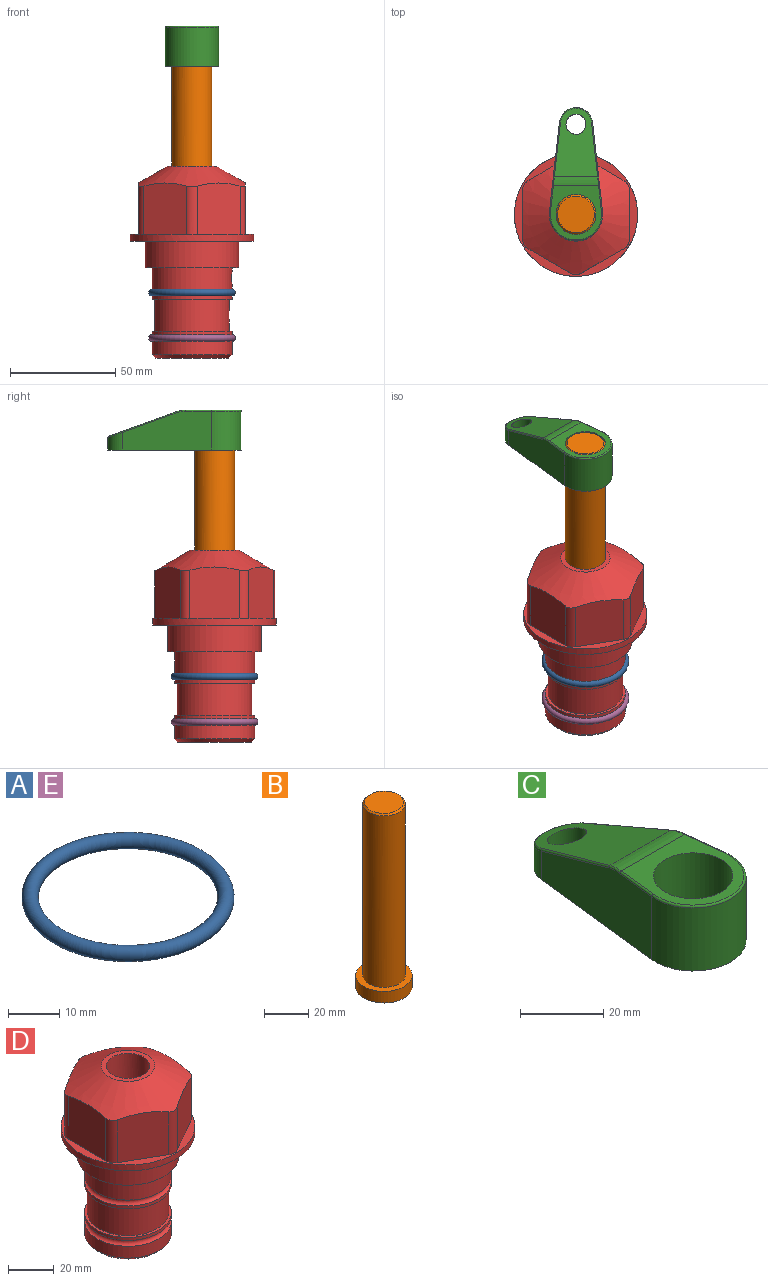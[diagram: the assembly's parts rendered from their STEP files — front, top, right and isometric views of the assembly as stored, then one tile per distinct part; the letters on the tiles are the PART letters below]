
ASSEMBLY  parts=5 mates=3
PART A: 1 faces, bbox 44.7x44.7x3.2 mm
  f0: torus R=19.05mm, axis (0,0,1), area 1193.9mm2
PART B: 6 faces, bbox 25.4x25.4x101.6 mm
  f0: plane 17.46x17.46mm, normal (0,0,1), area 239.5mm2, adj f5
  f1: plane 25.4x25.4mm, normal (0,0,-1), area 506.7mm2, adj f2
  f2: cylinder r=12.7mm len=25.4mm, axis (0,0,1), area 506.7mm2, adj f1,f3
  f3: plane 25.4x25.4mm, normal (0,0,1), area 221.7mm2, adj f2,f4
  f4: cylinder r=9.53mm len=94.46mm, axis (0,0,1), area 5653mm2, adj f3,f5
  f5: cone r=8.73mm half-angle=45deg, axis (0,0,-1), area 64.4mm2, adj f0,f4
PART C: 44 faces, bbox 27.5x64.5x19.1 mm
  f0: plane 2.3x0.95mm, normal (0,0,-1), area 1mm2, adj f25,f30,f34
  f1: plane 63.5x25.4mm, normal (0,0,-1), area 561.7mm2, adj f2,f3,f4,f5,f6,f7,f19,f20
  f2: cylinder r=12.7mm len=25.4mm, axis (0,0,-1), area 792.2mm2, adj f1,f3,f5,f13
  f3: plane 42.33x18.54mm, normal (0.99,0.11,0), area 647mm2, adj f1,f2,f4,f11,f12,f14
  f4: cylinder r=7.94mm len=15.78mm, axis (0,0,-1), area 158.6mm2, adj f1,f3,f5,f16
  f5: plane 42.33x18.54mm, normal (-0.99,0.11,0), area 647mm2, adj f1,f2,f4,f15,f17,f18
  f6: cylinder r=9.53mm len=19.05mm, axis (0,0,-1), area 1140.1mm2, adj f1,f8
  f7: cylinder r=4.76mm len=10.98mm, axis (0,0,-1), area 276.1mm2, adj f1,f9
  f8: plane 25.83x24.38mm, normal (0,0,1), area 262.2mm2, adj f6,f10,f11,f13,f15
  f9: plane 32.49x20.55mm, normal (0,0.34,0.94), area 489.9mm2, adj f7,f10,f14,f16,f18
  f10: cylinder r=12.7mm len=21.49mm, axis (-1,0,0), area 93.2mm2, adj f8,f9,f12,f17
  f11: cylinder r=0.51mm len=12.34mm, axis (0.11,-0.99,0), area 9.9mm2, adj f3,f8,f12,f13
  f12: bspline ~7.62x1.64mm, area 3.5mm2, adj f3,f10,f11,f14
  f13: torus R=12.19mm, axis (0,0,1), area 33.6mm2, adj f2,f8,f11,f15
  f14: cylinder r=0.51mm len=26.01mm, axis (0.1,-0.93,0.34), area 21.6mm2, adj f3,f9,f12,f16
  f15: cylinder r=0.51mm len=12.34mm, axis (0.11,0.99,0), area 9.9mm2, adj f5,f8,f13,f17
  f16: bspline ~15.78x7.05mm, area 15.7mm2, adj f4,f9,f14,f18
  f17: bspline ~7.62x1.64mm, area 3.5mm2, adj f5,f10,f15,f18
  f18: cylinder r=0.51mm len=26.01mm, axis (0.1,0.93,-0.34), area 21.6mm2, adj f5,f9,f16,f17
  f19: plane 21.6x14.29mm, normal (-0.99,-0.11,0), area 242.6mm2, adj f1,f26,f28,f34,f36,f38
  f20: plane 21.6x14.29mm, normal (0.99,-0.11,0), area 242.6mm2, adj f1,f27,f29,f37,f39,f41
  f21: cylinder r=12.7mm len=14.29mm, axis (0,0,-1), area 173.2mm2, adj f1,f26,f27,f30,f31,f33
  f22: cylinder r=7.94mm len=7.63mm, axis (0,0,-1), area 53.8mm2, adj f1,f28,f29,f42
  f23: plane 2.3x0.95mm, normal (0,0,-1), area 1mm2, adj f25,f33,f37
  f24: plane 17.94x12.32mm, normal (0,-0.34,-0.94), area 191.2mm2, adj f25,f38,f41,f42
  f25: cylinder r=9.53mm len=12.93mm, axis (-1,0,0), area 37.5mm2, adj f0,f23,f24,f31,f36,f39
  f26: cylinder r=1.59mm len=14.29mm, axis (0,0,-1), area 49mm2, adj f1,f19,f21,f32
  f27: cylinder r=1.59mm len=14.29mm, axis (0,0,-1), area 49mm2, adj f1,f20,f21,f35
  f28: cylinder r=1.59mm len=7.28mm, axis (0,0,-1), area 22.1mm2, adj f1,f19,f22,f40
  f29: cylinder r=1.59mm len=7.28mm, axis (0,0,-1), area 22.1mm2, adj f1,f20,f22,f43
  f30: torus R=14.29mm, axis (0,0,1), area 5.8mm2, adj f0,f21,f31,f32
  f31: bspline ~11.06x2.73mm, area 20.8mm2, adj f21,f25,f30,f33
  f32: sphere r=1.59mm, area 5.4mm2, adj f26,f30,f34
  f33: torus R=14.29mm, axis (0,0,1), area 5.8mm2, adj f21,f23,f31,f35
  f34: cylinder r=1.59mm len=1.68mm, axis (-0.11,0.99,0), area 2.4mm2, adj f0,f19,f32,f36
  f35: sphere r=1.59mm, area 5.4mm2, adj f27,f33,f37
  f36: bspline ~5.82x2.33mm, area 7.7mm2, adj f19,f25,f34,f38
  f37: cylinder r=1.59mm len=1.68mm, axis (0.11,0.99,0), area 2.4mm2, adj f20,f23,f35,f39
  f38: cylinder r=1.59mm len=18.33mm, axis (0.1,-0.93,0.34), area 46.7mm2, adj f19,f24,f36,f40
  f39: bspline ~5.82x2.33mm, area 7.7mm2, adj f20,f25,f37,f41
  f40: sphere r=1.59mm, area 3.6mm2, adj f28,f38,f42
  f41: cylinder r=1.59mm len=18.33mm, axis (0.1,0.93,-0.34), area 46.7mm2, adj f20,f24,f39,f43
  f42: bspline ~8.31x1.84mm, area 15.3mm2, adj f22,f24,f40,f43
  f43: sphere r=1.59mm, area 3.6mm2, adj f29,f41,f42
PART D: 36 faces, bbox 58.7x58.7x91.2 mm
  f0: cylinder r=17.78mm len=35.56mm, axis (0,0,1), area 1670.8mm2, adj f23,f24,f31
  f1: cylinder r=19.05mm len=38.1mm, axis (0,0,1), area 1191.9mm2, adj f26,f27,f30
  f2: plane 58.66x58.66mm, normal (0,0,-1), area 1150.6mm2, adj f3,f28
  f3: cylinder r=29.33mm len=58.66mm, axis (0,0,-1), area 585.1mm2, adj f2,f4
  f4: plane 58.66x58.66mm, normal (0,0,1), area 475.9mm2, adj f3,f5,f6,f7,f8,f9,f10,f11
  f5: plane 24.5x20.32mm, normal (0.5,-0.87,0), area 562.8mm2, adj f4,f15,f16,f17
  f6: plane 24.5x20.32mm, normal (-0.5,-0.87,0), area 562.8mm2, adj f4,f14,f15,f17
  f7: plane 24.5x23.48mm, normal (-1,0,0), area 562.8mm2, adj f4,f13,f14,f17
  f8: plane 24.5x20.32mm, normal (-0.5,0.87,0), area 562.8mm2, adj f4,f12,f13,f17
  f9: plane 24.5x20.32mm, normal (0.5,0.87,0), area 562.8mm2, adj f4,f11,f12,f17
  f10: plane 24.5x23.48mm, normal (1,0,0), area 562.8mm2, adj f4,f11,f16,f17
  f11: cylinder r=5.08mm len=23.01mm, axis (0,0,-1), area 121.2mm2, adj f4,f9,f10,f17
  f12: cylinder r=5.08mm len=23.01mm, axis (0,0,-1), area 121.2mm2, adj f4,f8,f9,f17
  f13: cylinder r=5.08mm len=23.01mm, axis (0,0,-1), area 121.2mm2, adj f4,f7,f8,f17
  f14: cylinder r=5.08mm len=23.01mm, axis (0,0,-1), area 121.2mm2, adj f4,f6,f7,f17
  f15: cylinder r=5.08mm len=23.01mm, axis (0,0,-1), area 121.2mm2, adj f4,f5,f6,f17
  f16: cylinder r=5.08mm len=23.01mm, axis (0,0,-1), area 121.2mm2, adj f4,f5,f10,f17
  f17: cone r=11.73mm half-angle=60deg, axis (0,0,-1), area 2071.8mm2, adj f5,f6,f7,f8,f9,f10,f11,f12
  f18: plane 23.46x23.46mm, normal (0,0,1), area 147.4mm2, adj f17,f35
  f19: plane 34.93x34.93mm, normal (0,0,-1), area 958mm2, adj f29
  f20: cylinder r=19.05mm len=38.1mm, axis (0,0,1), area 760.1mm2, adj f21,f29
  f21: torus R=19.05mm, axis (0,0,1), area 565.3mm2, adj f20,f22
  f22: cylinder r=19.05mm len=38.1mm, axis (0,0,1), area 190mm2, adj f21,f23
  f23: plane 38.1x38.1mm, normal (0,0,1), area 146.9mm2, adj f0,f22
  f24: plane 38.1x38.1mm, normal (0,0,-1), area 146.9mm2, adj f0,f25
  f25: cylinder r=19.05mm len=38.1mm, axis (0,0,1), area 190mm2, adj f24,f26
  f26: torus R=19.05mm, axis (0,0,1), area 565.3mm2, adj f1,f25
  f27: plane 44.45x44.45mm, normal (0,0,-1), area 411.7mm2, adj f1,f28
  f28: cylinder r=22.23mm len=44.45mm, axis (0,0,1), area 1773.5mm2, adj f2,f27
  f29: cone r=19.05mm half-angle=45deg, axis (0,0,1), area 257.5mm2, adj f19,f20
  f30: cylinder r=3.17mm len=6.75mm, axis (-1,0,0), area 128mm2, adj f1,f33
  f31: cylinder r=3.17mm len=6.35mm, axis (-1,0,0), area 102.5mm2, adj f0,f33
  f32: plane 25.4x25.4mm, normal (0,0,1), area 506.7mm2, adj f33
  f33: cylinder r=12.7mm len=66.42mm, axis (0,0,-1), area 5236.2mm2, adj f30,f31,f32,f34
  f34: cone r=9.53mm half-angle=30deg, axis (0,0,-1), area 443.4mm2, adj f33,f35
  f35: cylinder r=9.53mm len=19.05mm, axis (0,0,-1), area 849mm2, adj f18,f34
PART E: same geometry as A
PLACE A t=(0,0,-1.88)mm
PLACE B t=(0,0,26.83)mm
PLACE C t=(0,0,81.44)mm
PLACE D t=(0,0,-1.88)mm
PLACE E t=(0,0,-23.47)mm
MATE revolute E.f0 <-> D.f0  axis (0,0,1) through (0,0,-47.98)mm
MATE cylindrical C.f2 <-> B.f2  axis (0,0,-1) through (0,0,100.49)mm
MATE slider B.f2 <-> D.f0  axis (0,0,1) through (0,0,52.47)mm
